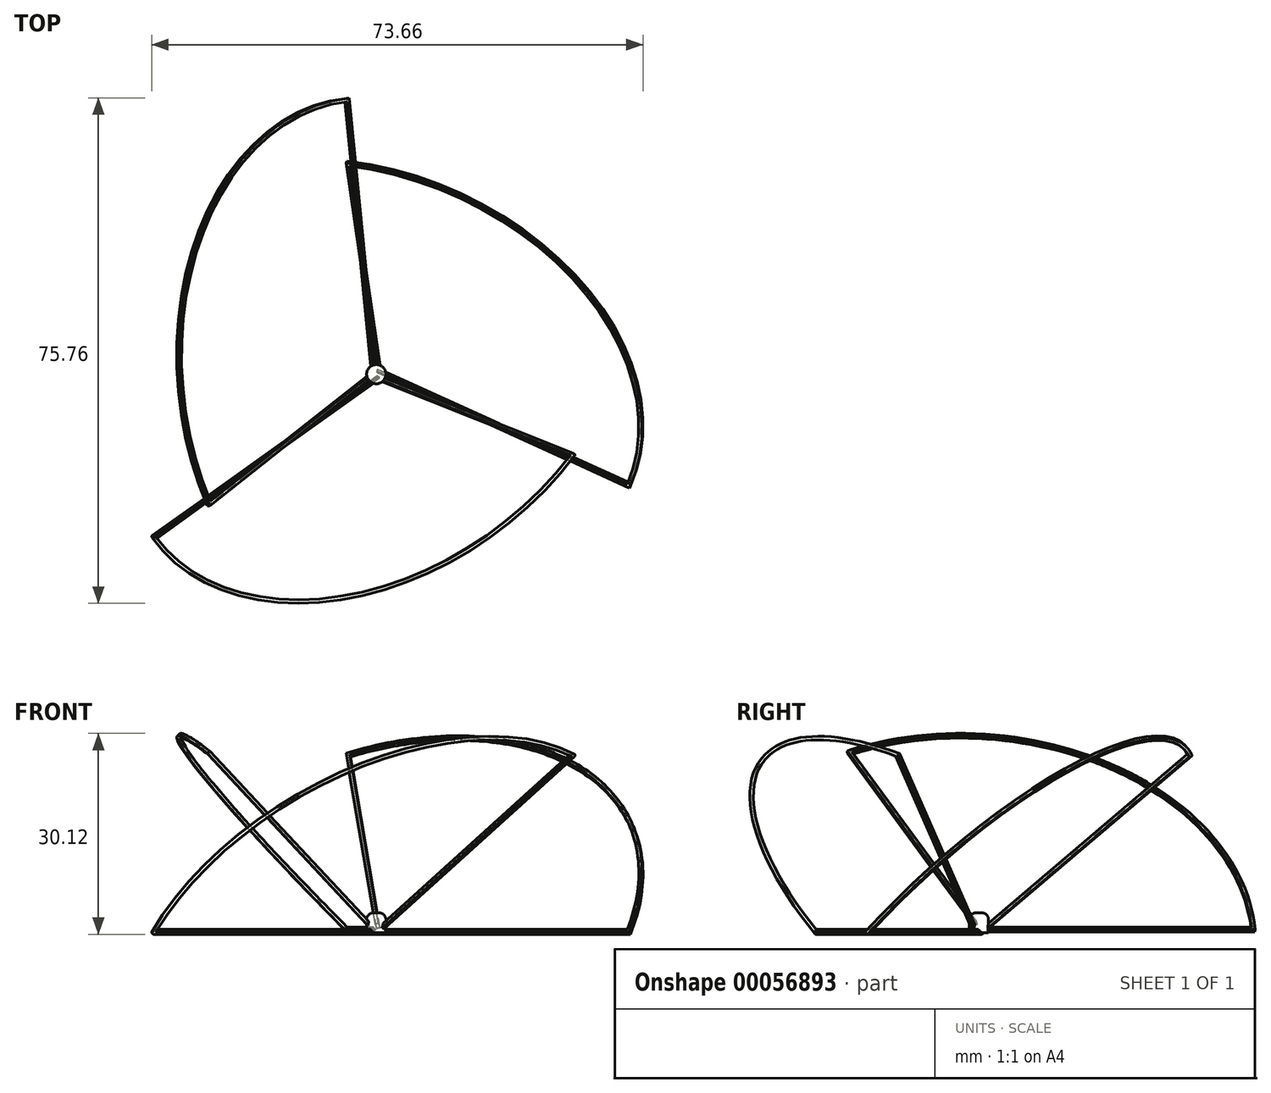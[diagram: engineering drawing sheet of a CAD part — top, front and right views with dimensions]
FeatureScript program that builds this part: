
annotation { "Feature Type Name" : "Feature", "Feature Type Description" : "" }
export const myFeature = defineFeature(function(context is Context, id is Id, definition is map)
    precondition{}
    {
        {
            var Q0;
            Q0=qCreatedBy(makeId("Top.planeOp"),FACE);
            var sketch = newSketch(context, id + "F0", { "sketchPlane" : qUnion([Q0])});
            skLineSegment(sketch, "E0", {"start": v(0, 0) * mm, "end": v(0, 41.6) * mm});
            skLineSegment(sketch, "E1.2.0", {"start": v(0, 0) * mm, "end": v(37.88, -17.18) * mm});
            skPoint(sketch, "E1.center", {"position": v(0, 0) * mm});
            skArc(sketch, "E2", {"start": v(0, 41.6) * mm, "mid": v(34.96, 22.53) * mm, "end": v(37.88, -17.18) * mm});
            skLineSegment(sketch, "E3.1.1", {"start": v(0, 0) * mm, "end": v(-36.02, -20.8) * mm});
            skLineSegment(sketch, "E3.1.2", {"start": v(0, 0) * mm, "end": v(-4.06, 41.4) * mm});
            skArc(sketch, "E3.1.3", {"start": v(-36.02, -20.8) * mm, "mid": v(-37, 19.01) * mm, "end": v(-4.06, 41.4) * mm});
            skLineSegment(sketch, "E3.2.1", {"start": v(0, 0) * mm, "end": v(36.02, -20.8) * mm});
            skLineSegment(sketch, "E3.2.2", {"start": v(0, 0) * mm, "end": v(-33.82, -24.21) * mm});
            skArc(sketch, "E3.2.3", {"start": v(36.02, -20.8) * mm, "mid": v(2.03, -41.55) * mm, "end": v(-33.82, -24.21) * mm});
            skLineSegment(sketch, "E4.0", {"start": v(0.5, 0.32) * mm, "end": v(0.5, 4.02) * mm});
            skLineSegment(sketch, "E4.1", {"start": v(0.5, 0.32) * mm, "end": v(5.08, -1.75) * mm});
            skArc(sketch, "E4.2", {"start": v(0.5, 41.1) * mm, "mid": v(34.54, 22.26) * mm, "end": v(37.63, -16.52) * mm});
            skLineSegment(sketch, "E5.0", {"start": v(-0.53, 0.27) * mm, "end": v(-1.06, 5.66) * mm});
            skLineSegment(sketch, "E5.1", {"start": v(-0.53, 0.27) * mm, "end": v(-6.63, -3.25) * mm});
            skArc(sketch, "E5.2", {"start": v(-35.84, -20.11) * mm, "mid": v(-36.55, 18.78) * mm, "end": v(-4.5, 40.85) * mm});
            skLineSegment(sketch, "E6.0", {"start": v(0.03, -0.6) * mm, "end": v(-6.44, -5.22) * mm});
            skLineSegment(sketch, "E6.1", {"start": v(0.03, -0.6) * mm, "end": v(10.18, -6.45) * mm});
            skArc(sketch, "E6.2", {"start": v(35.34, -20.98) * mm, "mid": v(2, -41.05) * mm, "end": v(-33.12, -24.33) * mm});
            skLineSegment(sketch, "E7", {"start": v(5.08, -1.75) * mm, "end": v(37.63, -16.52) * mm});
            skLineSegment(sketch, "E8", {"start": v(0.5, 4.02) * mm, "end": v(0.5, 41.1) * mm});
            skLineSegment(sketch, "E9", {"start": v(-1.06, 5.66) * mm, "end": v(-4.5, 40.85) * mm});
            skLineSegment(sketch, "E10", {"start": v(-6.63, -3.25) * mm, "end": v(-35.84, -20.11) * mm});
            skLineSegment(sketch, "E11", {"start": v(-6.44, -5.22) * mm, "end": v(-33.12, -24.33) * mm});
            skLineSegment(sketch, "E12", {"start": v(10.18, -6.45) * mm, "end": v(35.34, -20.98) * mm});
            skSolve(sketch);
        }
        {
            var Q0;
            Q0 = qSketchRegion(id + "F0", true);
            extrude(context, id + "F1", {"entities" : qUnion([Q0]), "depth" : .5 * mm});
        }
        {
            var Q0;
            Q0=makeQuery(id+"F1.opExtrude","SWEPT_BODY",BODY,{"disambiguationData":[OSD([sQuery(id+"F0.wireOp",EDGE,"E0"),sQuery(id+"F0.wireOp",EDGE,"E1.2.0"),sQuery(id+"F0.wireOp",EDGE,"E2"),sQuery(id+"F0.wireOp",EDGE,"E4.0"),sQuery(id+"F0.wireOp",EDGE,"E4.1"),sQuery(id+"F0.wireOp",EDGE,"E4.2"),sQuery(id+"F0.wireOp",EDGE,"E7"),sQuery(id+"F0.wireOp",EDGE,"E8")])]});
            var Q1;
            Q1=makeQuery(id+"F1.opExtrude","CAP_EDGE",EDGE,{"disambiguationData":[OSD([sQuery(id+"F0.wireOp",EDGE,"E4.1"),sQuery(id+"F0.wireOp",EDGE,"E7")])],"isStart":false});
            transform(context, id + "F2", {"entities" : qUnion([Q0]), "transformType" : TransformType.ROTATION, "transformAxis" : qUnion([Q1]), "angle" : 45 * degree, "makeCopy" : false});
        }
        {
            var Q0;
            Q0=makeQuery(id+"F1.opExtrude","SWEPT_BODY",BODY,{"disambiguationData":[OSD([sQuery(id+"F0.wireOp",EDGE,"E3.1.1"),sQuery(id+"F0.wireOp",EDGE,"E3.1.2"),sQuery(id+"F0.wireOp",EDGE,"E3.1.3"),sQuery(id+"F0.wireOp",EDGE,"E5.0"),sQuery(id+"F0.wireOp",EDGE,"E5.1"),sQuery(id+"F0.wireOp",EDGE,"E5.2"),sQuery(id+"F0.wireOp",EDGE,"E9"),sQuery(id+"F0.wireOp",EDGE,"E10")])]});
            var Q1;
            Q1=makeQuery(id+"F1.opExtrude","CAP_EDGE",EDGE,{"disambiguationData":[OSD([sQuery(id+"F0.wireOp",EDGE,"E3.1.2")])],"isStart":false});
            transform(context, id + "F3", {"entities" : qUnion([Q0]), "transformType" : TransformType.ROTATION, "transformAxis" : qUnion([Q1]), "angle" : 45 * degree, "makeCopy" : false});
        }
        {
            var Q0;
            Q0=makeQuery(id+"F1.opExtrude","SWEPT_BODY",BODY,{"disambiguationData":[OSD([sQuery(id+"F0.wireOp",EDGE,"E3.2.1"),sQuery(id+"F0.wireOp",EDGE,"E3.2.2"),sQuery(id+"F0.wireOp",EDGE,"E3.2.3"),sQuery(id+"F0.wireOp",EDGE,"E6.0"),sQuery(id+"F0.wireOp",EDGE,"E6.1"),sQuery(id+"F0.wireOp",EDGE,"E6.2"),sQuery(id+"F0.wireOp",EDGE,"E11"),sQuery(id+"F0.wireOp",EDGE,"E12")])]});
            var Q1;
            Q1=makeQuery(id+"F1.opExtrude","CAP_EDGE",EDGE,{"disambiguationData":[OSD([sQuery(id+"F0.wireOp",EDGE,"E6.0"),sQuery(id+"F0.wireOp",EDGE,"E11")])],"isStart":false});
            transform(context, id + "F4", {"entities" : qUnion([Q0]), "transformType" : TransformType.ROTATION, "transformAxis" : qUnion([Q1]), "angle" : 45 * degree, "makeCopy" : false});
        }
        {
            var Q0;
            Q0=qCreatedBy(makeId("Top.planeOp"),FACE);
            var sketch = newSketch(context, id + "F5", { "sketchPlane" : qUnion([Q0])});
            skCircle(sketch, "E13", {"center": v(0, 0) * mm, "radius": 1.44 * mm});
            skSolve(sketch);
        }
        {
            var Q0;
            Q0 = qSketchRegion(id + "F5", true);
            extrude(context, id + "F6", {"entities" : qUnion([Q0]), "operationType" : NewBodyOperationType.ADD, "depth" : 3 * mm});
        }
        {
            var Q0;
            Q0=makeQuery(id+"F6.opExtrude","CAP_EDGE",EDGE,{"disambiguationData":[OSD([sQuery(id+"F5.wireOp",EDGE,"E13")])],"isStart":false});
            fillet(context, id + "F7", {"entities" : qUnion([Q0]), "radius" : 1 * mm, "tangentPropagation" : true, "allowEdgeOverflow" : false});
        }
        {
            var Q0;
            Q0=makeQuery(id+"F1.opExtrude","CAP_EDGE",EDGE,{"disambiguationData":[OSD([sQuery(id+"F0.wireOp",EDGE,"E3.2.3")])],"isStart":true});
            var Q1;
            Q1=makeQuery(id+"F1.opExtrude","CAP_EDGE",EDGE,{"disambiguationData":[OSD([sQuery(id+"F0.wireOp",EDGE,"E3.2.3")])],"isStart":false});
            var Q2;
            Q2=makeQuery(id+"F1.opExtrude","CAP_EDGE",EDGE,{"disambiguationData":[OSD([sQuery(id+"F0.wireOp",EDGE,"E6.2")])],"isStart":false});
            var Q3;
            Q3=makeQuery(id+"F1.opExtrude","CAP_EDGE",EDGE,{"disambiguationData":[OSD([sQuery(id+"F0.wireOp",EDGE,"E6.2")])],"isStart":true});
            fillet(context, id + "F8", {"entities" : qUnion([Q0, Q1, Q2, Q3]), "radius" : .2 * mm, "tangentPropagation" : true, "allowEdgeOverflow" : false});
        }
    });
